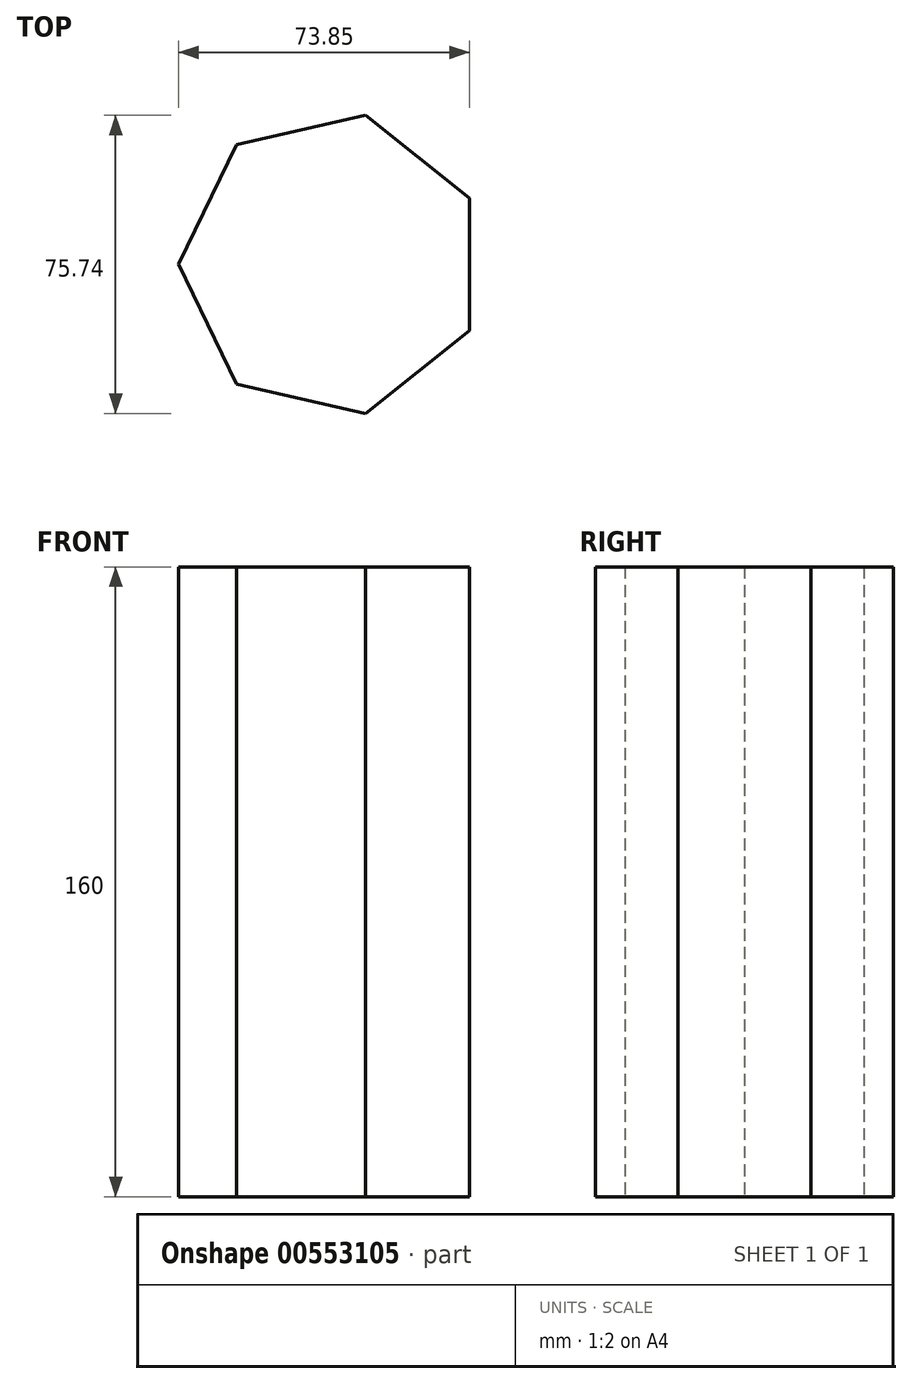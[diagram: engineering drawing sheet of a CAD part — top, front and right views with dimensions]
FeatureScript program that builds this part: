
annotation { "Feature Type Name" : "Feature", "Feature Type Description" : "" }
export const myFeature = defineFeature(function(context is Context, id is Id, definition is map)
    precondition{}
    {
        {
            var Q0;
            Q0=qCreatedBy(makeId("Top.planeOp"),FACE);
            var sketch = newSketch(context, id + "F0", { "sketchPlane" : qUnion([Q0])});
            skCircle(sketch, "E0.cCircle", {"center": v(0, 0) * mm, "radius": 35 * mm, "construction": true});
            skLineSegment(sketch, "E0.0", {"start": v(35, 16.86) * mm, "end": v(35, -16.86) * mm});
            skLineSegment(sketch, "E0.1", {"start": v(35, -16.86) * mm, "end": v(8.64, -37.87) * mm});
            skLineSegment(sketch, "E0.2", {"start": v(8.64, -37.87) * mm, "end": v(-24.22, -30.37) * mm});
            skLineSegment(sketch, "E0.3", {"start": v(-24.22, -30.37) * mm, "end": v(-38.85, 0) * mm});
            skLineSegment(sketch, "E0.4", {"start": v(-38.85, 0) * mm, "end": v(-24.22, 30.37) * mm});
            skLineSegment(sketch, "E0.5", {"start": v(-24.22, 30.37) * mm, "end": v(8.64, 37.87) * mm});
            skLineSegment(sketch, "E0.6", {"start": v(8.64, 37.87) * mm, "end": v(35, 16.86) * mm});
            skPoint(sketch, "E0.0.midPoint", {"position": v(35, 0) * mm});
            skSolve(sketch);
        }
        {
            var Q0;
            Q0=makeQuery(id+"F0.imprint","IMPRINT",FACE,{"disambiguationData":[TD([[makeQuery(id+"F0.imprint","IMPRINT",EDGE,{"derivedFrom":sQuery(id+"F0.wireOp",EDGE,"E0.0")}),-1.0]])]});
            extrude(context, id + "F1", {"entities" : qUnion([Q0]), "depth" : 160 * mm, "offsetDistance" : 25 * mm});
        }
    });
